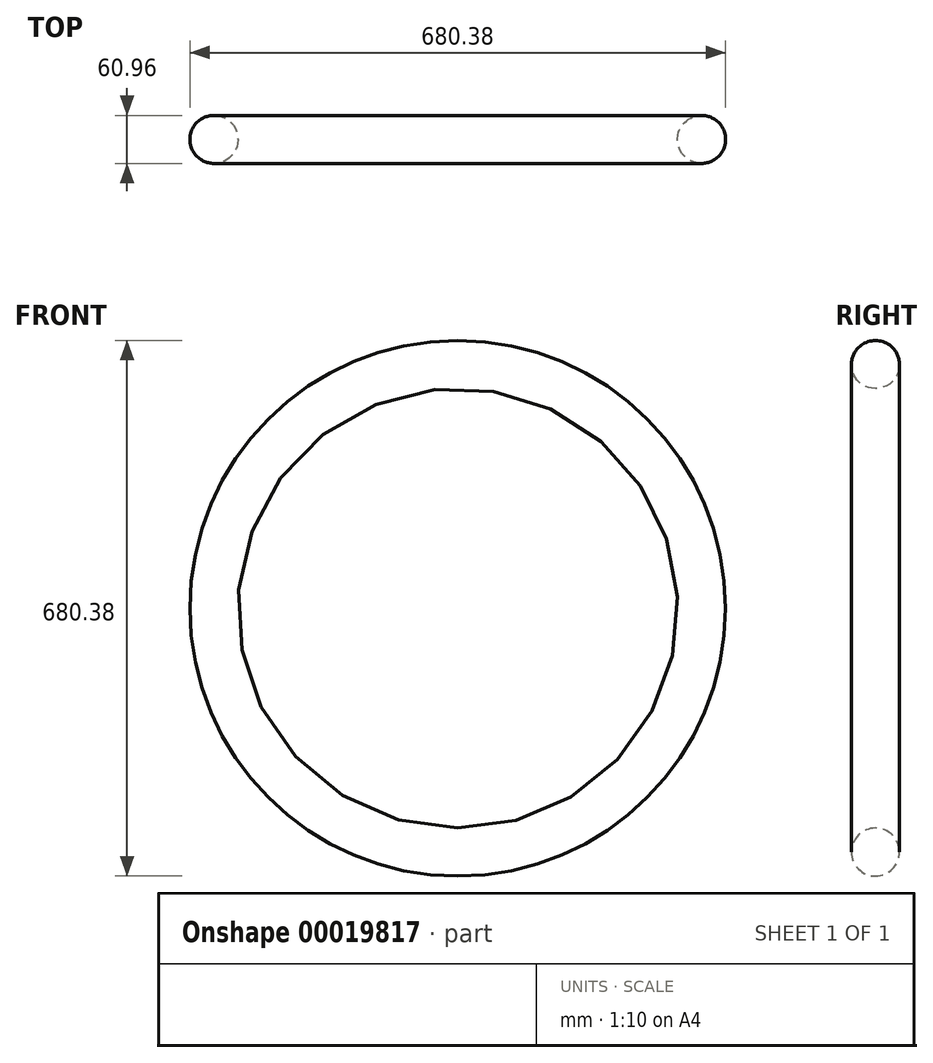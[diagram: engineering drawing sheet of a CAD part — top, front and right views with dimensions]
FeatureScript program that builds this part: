
annotation { "Feature Type Name" : "Feature", "Feature Type Description" : "" }
export const myFeature = defineFeature(function(context is Context, id is Id, definition is map)
    precondition{}
    {
        {
            var Q0;
            Q0=qCreatedBy(makeId("Top.planeOp"),FACE);
            var sketch = newSketch(context, id + "F0", { "sketchPlane" : qUnion([Q0])});
            skCircle(sketch, "E0", {"center": v(309.7, 0) * mm, "radius": 30.48 * mm});
            skPoint(sketch, "E1", {"position": v(279.23, 0) * mm});
            skLineSegment(sketch, "E2", {"start": v(0, 0) * mm, "end": v(0, 53.37) * mm, "construction": true});
            skPoint(sketch, "E3", {"position": v(340.2, 0) * mm});
            skSolve(sketch);
        }
        {
            var Q0;
            Q0 = qSketchRegion(id + "F0", true);
            var Q1;
            Q1=sQuery(id+"F0.wireOp",EDGE,"E2");
            revolve(context, id + "F1", {"entities" : qUnion([Q0]), "axis" : qUnion([Q1]), "revolveType" : RevolveType.FULL});
        }
    });
